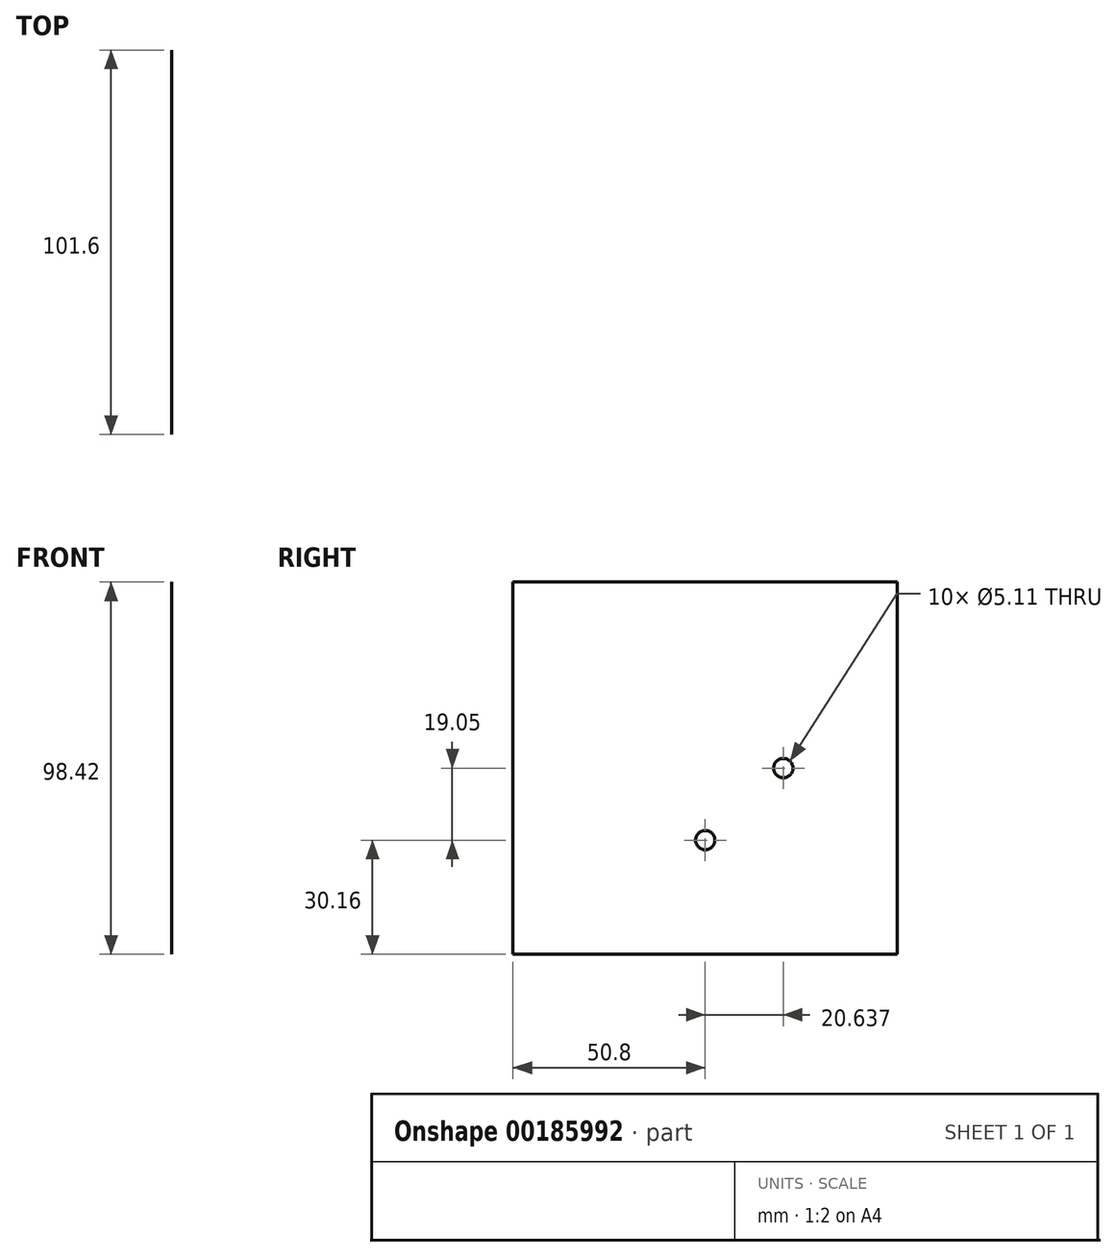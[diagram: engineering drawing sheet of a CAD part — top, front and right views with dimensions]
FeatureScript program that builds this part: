
annotation { "Feature Type Name" : "Feature", "Feature Type Description" : "" }
export const myFeature = defineFeature(function(context is Context, id is Id, definition is map)
    precondition{}
    {
        {
            var Q0;
            Q0=qCreatedBy(makeId("Right.planeOp"),FACE);
            var sketch = newSketch(context, id + "F0", { "sketchPlane" : qUnion([Q0])});
            skLineSegment(sketch, "E0.bottom", {"start": v(50.8, -49.21) * mm, "end": v(-50.8, -49.21) * mm});
            skLineSegment(sketch, "E0.top", {"start": v(50.8, 49.21) * mm, "end": v(-50.8, 49.21) * mm});
            skLineSegment(sketch, "E0.left", {"start": v(50.8, -49.21) * mm, "end": v(50.8, 49.21) * mm});
            skLineSegment(sketch, "E0.right", {"start": v(-50.8, -49.21) * mm, "end": v(-50.8, 49.21) * mm});
            skPoint(sketch, "E0.middle", {"position": v(0, 0) * mm});
            skSolve(sketch);
        }
        {
            var Q0;
            Q0 = qSketchRegion(id + "F0", true);
            extrude(context, id + "F1", {"entities" : qUnion([Q0]), "depth" : 1 / 203.2 * mm});
        }
        {
            var Q0;
            Q0=makeQuery(id+"F1.opExtrude","CAP_FACE",FACE,{"disambiguationData":[OSD([sQuery(id+"F0.wireOp",EDGE,"E0.bottom"),sQuery(id+"F0.wireOp",EDGE,"E0.top"),sQuery(id+"F0.wireOp",EDGE,"E0.left"),sQuery(id+"F0.wireOp",EDGE,"E0.right")])],"isStart":false});
            var sketch = newSketch(context, id + "F2", { "sketchPlane" : qUnion([Q0])});
            skPoint(sketch, "E1", {"position": v(0, -19.05) * mm});
            skPoint(sketch, "E2", {"position": v(20.64, 0) * mm});
            skPoint(sketch, "E2.positionSnap0", {"position": v(50.8, 0) * mm});
            skSolve(sketch);
        }
        {
            var Q0;
            Q0=sQuery(id+"F2.wireOp",VERTEX,"E1");
            var Q1;
            Q1=sQuery(id+"F2.wireOp",VERTEX,"E2");
            var Q2;
            Q2=makeQuery(id+"F1.opExtrude","SWEPT_BODY",BODY,{"disambiguationData":[OSD([sQuery(id+"F0.wireOp",EDGE,"E0.bottom"),sQuery(id+"F0.wireOp",EDGE,"E0.top"),sQuery(id+"F0.wireOp",EDGE,"E0.left"),sQuery(id+"F0.wireOp",EDGE,"E0.right")])]});
            hole(context, id + "F3", {"style" : HoleStyle.SIMPLE, "endStyle" : HoleEndStyle.BLIND, "standardTappedOrClearance" : lookupTablePath({ "standard" : "ANSI", "fit" : "Normal (ASME)", "size" : "#10", "type" : "Clearance" }), "standardBlindInLast" : lookupTablePath({ "fit" : "Free", "standard" : "ANSI", "size" : "#10", "type" : "Clearance" }), "holeDiameter" : 5.1 * mm, "holeDepth" : 25 * mm, "locations" : qUnion([Q0, Q1]), "scope" : qUnion([Q2])});
        }
    });
